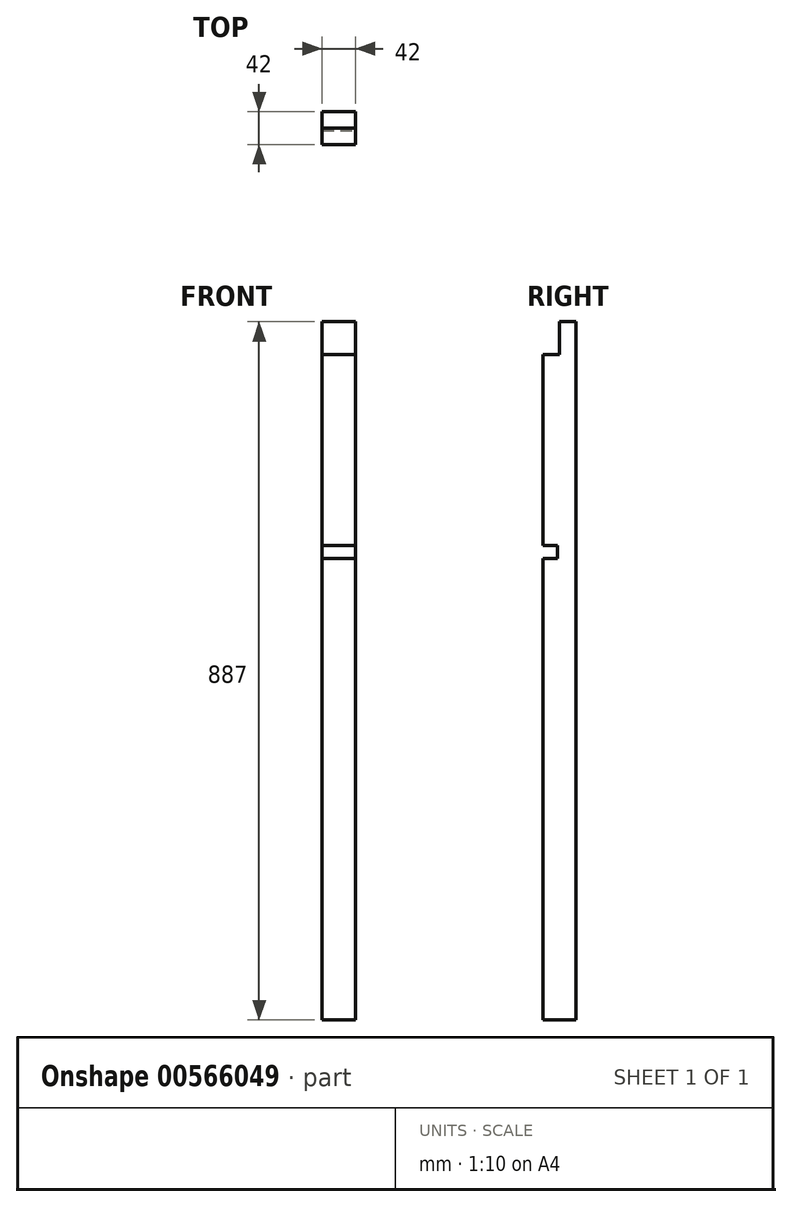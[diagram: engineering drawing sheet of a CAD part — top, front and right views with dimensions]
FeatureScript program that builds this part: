
annotation { "Feature Type Name" : "Feature", "Feature Type Description" : "" }
export const myFeature = defineFeature(function(context is Context, id is Id, definition is map)
    precondition{}
    {
        {
            var Q0;
            Q0=qCreatedBy(makeId("Top.planeOp"),FACE);
            var sketch = newSketch(context, id + "F0", { "sketchPlane" : qUnion([Q0])});
            skLineSegment(sketch, "E0.bottom", {"start": v(-55.79, 37.72) * mm, "end": v(-13.79, 37.72) * mm});
            skLineSegment(sketch, "E0.top", {"start": v(-55.79, -4.28) * mm, "end": v(-13.79, -4.28) * mm});
            skLineSegment(sketch, "E0.left", {"start": v(-55.79, 37.72) * mm, "end": v(-55.79, -4.28) * mm});
            skLineSegment(sketch, "E0.right", {"start": v(-13.79, 37.72) * mm, "end": v(-13.79, -4.28) * mm});
            skSolve(sketch);
        }
        {
            var Q0;
            Q0 = qSketchRegion(id + "F0", true);
            extrude(context, id + "F1", {"entities" : qUnion([Q0]), "depth" : 887 * mm, "offsetDistance" : 25 * mm});
        }
        {
            var Q0;
            Q0=makeQuery(id+"F1.opExtrude","SWEPT_FACE",FACE,{"disambiguationData":[OSD([sQuery(id+"F0.wireOp",EDGE,"E0.right")])]});
            var sketch = newSketch(context, id + "F2", { "sketchPlane" : qUnion([Q0])});
            skLineSegment(sketch, "E1.bottom", {"start": v(16.72, 887) * mm, "end": v(-4.28, 887) * mm});
            skLineSegment(sketch, "E1.top", {"start": v(16.72, 845.4) * mm, "end": v(-4.28, 845.4) * mm});
            skLineSegment(sketch, "E1.left", {"start": v(16.72, 887) * mm, "end": v(16.72, 845.4) * mm});
            skLineSegment(sketch, "E1.right", {"start": v(-4.28, 887) * mm, "end": v(-4.28, 845.4) * mm});
            skSolve(sketch);
        }
        {
            var Q0;
            Q0 = qSketchRegion(id + "F2", true);
            extrude(context, id + "F3", {"entities" : qUnion([Q0]), "operationType" : NewBodyOperationType.REMOVE, "oppositeDirection" : true, "depth" : 42 * mm, "offsetDistance" : 25 * mm});
        }
        {
            var Q0;
            Q0=makeQuery(id+"F1.opExtrude","SWEPT_FACE",FACE,{"disambiguationData":[OSD([sQuery(id+"F0.wireOp",EDGE,"E0.right")])]});
            var sketch = newSketch(context, id + "F4", { "sketchPlane" : qUnion([Q0])});
            skLineSegment(sketch, "E2.bottom", {"start": v(-4.28, 585.99) * mm, "end": v(13.72, 585.99) * mm});
            skLineSegment(sketch, "E2.top", {"start": v(-4.28, 602.99) * mm, "end": v(13.72, 602.99) * mm});
            skLineSegment(sketch, "E2.left", {"start": v(-4.28, 585.99) * mm, "end": v(-4.28, 602.99) * mm});
            skLineSegment(sketch, "E2.right", {"start": v(13.72, 585.99) * mm, "end": v(13.72, 602.99) * mm});
            skSolve(sketch);
        }
        {
            var Q0;
            Q0=makeQuery(id+"F4.imprint","IMPRINT",FACE,{"disambiguationData":[TD([[makeQuery(id+"F4.imprint","IMPRINT",EDGE,{"derivedFrom":sQuery(id+"F4.wireOp",EDGE,"E2.bottom")}),1.0]])]});
            extrude(context, id + "F5", {"entities" : qUnion([Q0]), "operationType" : NewBodyOperationType.REMOVE, "oppositeDirection" : true, "depth" : 42 * mm, "offsetDistance" : 25 * mm});
        }
    });
